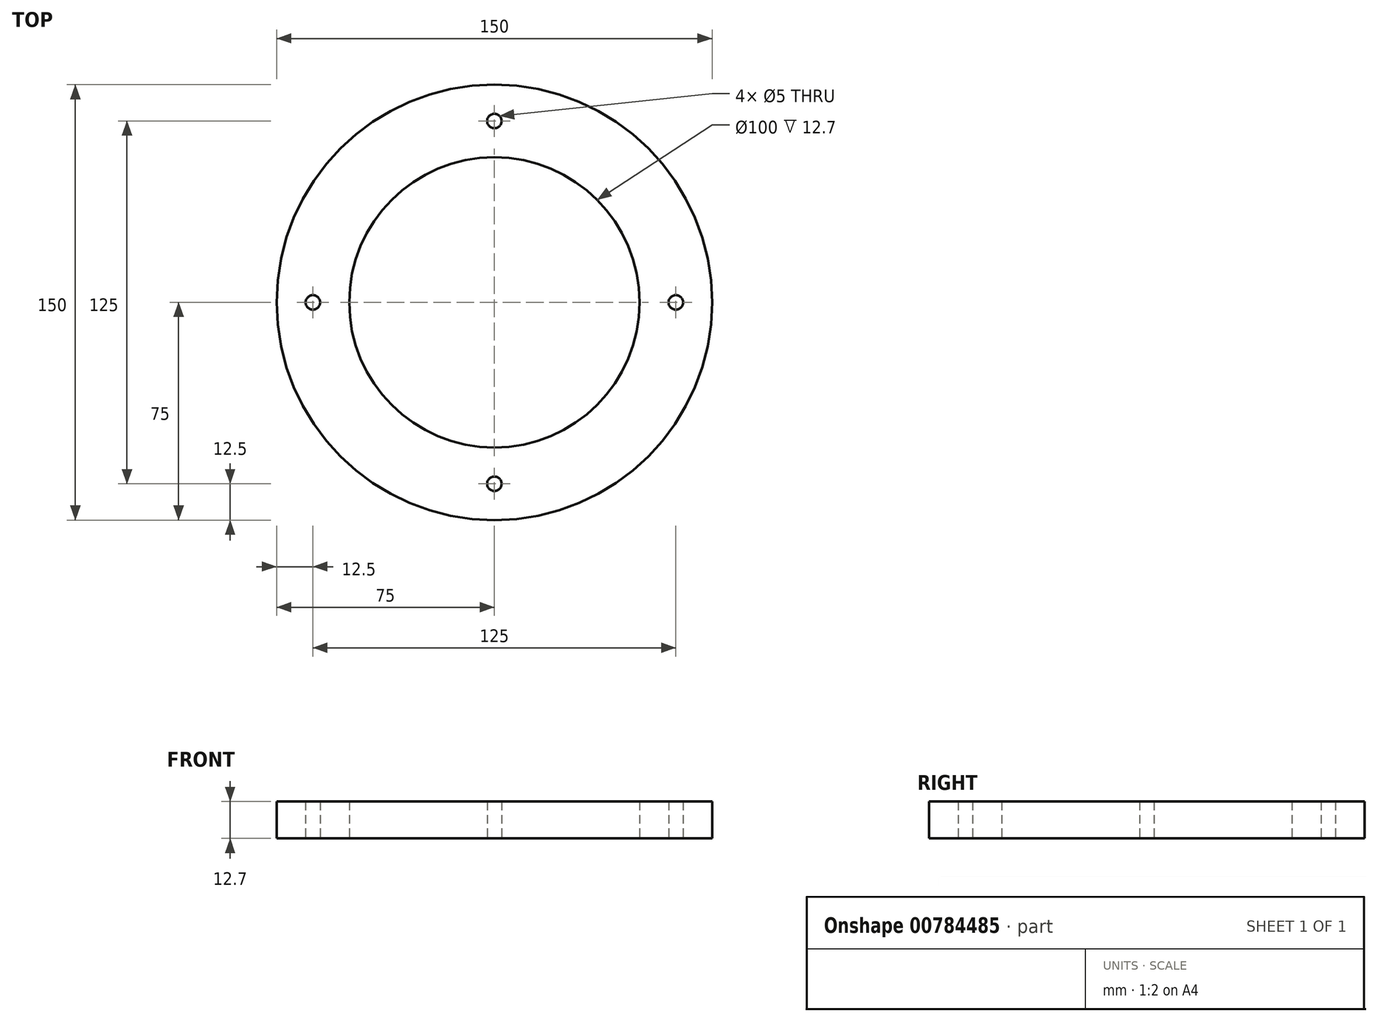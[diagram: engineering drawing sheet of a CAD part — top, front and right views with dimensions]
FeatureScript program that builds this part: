
annotation { "Feature Type Name" : "Feature", "Feature Type Description" : "" }
export const myFeature = defineFeature(function(context is Context, id is Id, definition is map)
    precondition{}
    {
        {
            var Q0;
            Q0=qCreatedBy(makeId("Top.planeOp"),FACE);
            var sketch = newSketch(context, id + "F0", { "sketchPlane" : qUnion([Q0])});
            skCircle(sketch, "E0", {"center": v(0, 0) * mm, "radius": 50 * mm});
            skCircle(sketch, "E1", {"center": v(0, 0) * mm, "radius": 75 * mm});
            skLineSegment(sketch, "E2", {"start": v(0, 0) * mm, "end": v(-62.5, 0) * mm});
            skLineSegment(sketch, "E3", {"start": v(0, 0) * mm, "end": v(0, 62.5) * mm});
            skLineSegment(sketch, "E4", {"start": v(0, 0) * mm, "end": v(62.5, 0) * mm});
            skLineSegment(sketch, "E5", {"start": v(0, 0) * mm, "end": v(0, -62.5) * mm});
            skCircle(sketch, "E6", {"center": v(-62.5, 0) * mm, "radius": 2.5 * mm});
            skCircle(sketch, "E7", {"center": v(0, 62.5) * mm, "radius": 2.5 * mm});
            skCircle(sketch, "E8", {"center": v(62.5, 0) * mm, "radius": 2.5 * mm});
            skCircle(sketch, "E9", {"center": v(0, -62.5) * mm, "radius": 2.5 * mm});
            skSolve(sketch);
        }
        {
            var Q0;
            Q0=makeQuery(id+"F0.imprint","IMPRINT",FACE,{"disambiguationData":[TD([[makeQuery(id+"F0.imprint","IMPRINT",EDGE,{"derivedFrom":sQuery(id+"F0.wireOp",EDGE,"E1")}),1.0]])]});
            extrude(context, id + "F1", {"entities" : qUnion([Q0]), "depth" : 12.7 * mm, "offsetDistance" : 25.4 * mm});
        }
    });
